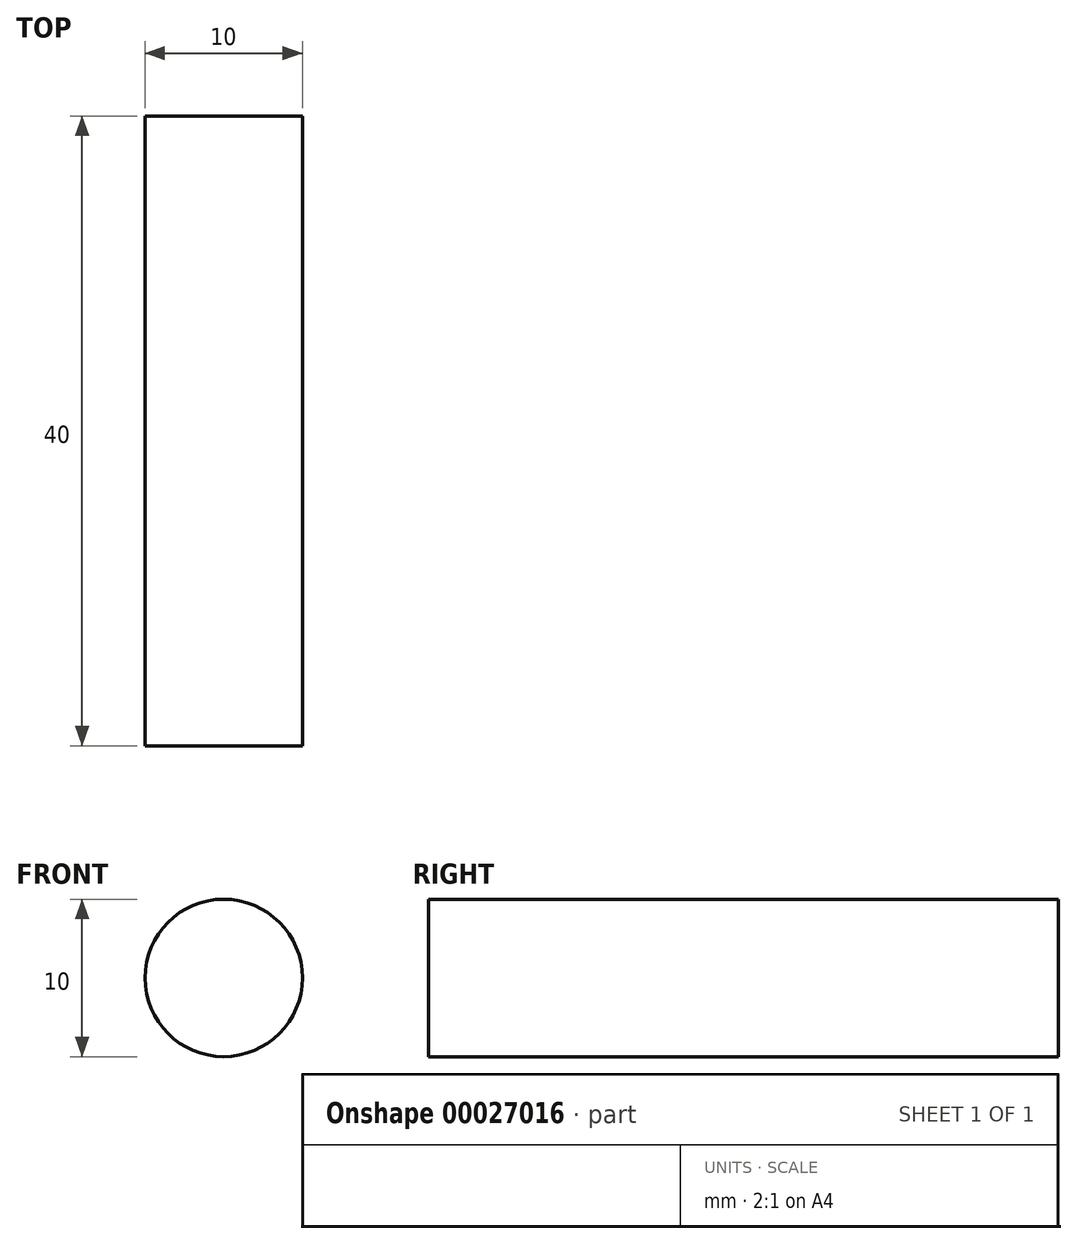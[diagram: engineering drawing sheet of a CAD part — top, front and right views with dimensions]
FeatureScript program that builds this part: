
annotation { "Feature Type Name" : "Feature", "Feature Type Description" : "" }
export const myFeature = defineFeature(function(context is Context, id is Id, definition is map)
    precondition{}
    {
        {
            var Q0;
            Q0=qCreatedBy(makeId("Front.planeOp"),FACE);
            var sketch = newSketch(context, id + "F0", { "sketchPlane" : qUnion([Q0])});
            skCircle(sketch, "E0", {"center": v(24.07, 20.84) * mm, "radius": 5 * mm});
            skSolve(sketch);
        }
        {
            var Q0;
            Q0=makeQuery(id+"F0.imprint","IMPRINT",FACE,{"disambiguationData":[TD([[makeQuery(id+"F0.imprint","IMPRINT",EDGE,{"derivedFrom":sQuery(id+"F0.wireOp",EDGE,"E0")}),1.0]])]});
            extrude(context, id + "F1", {"entities" : qUnion([Q0]), "depth" : 20 * mm, "hasSecondDirection" : true, "secondDirectionOppositeDirection" : true, "secondDirectionDepth" : 20 * mm});
        }
    });
